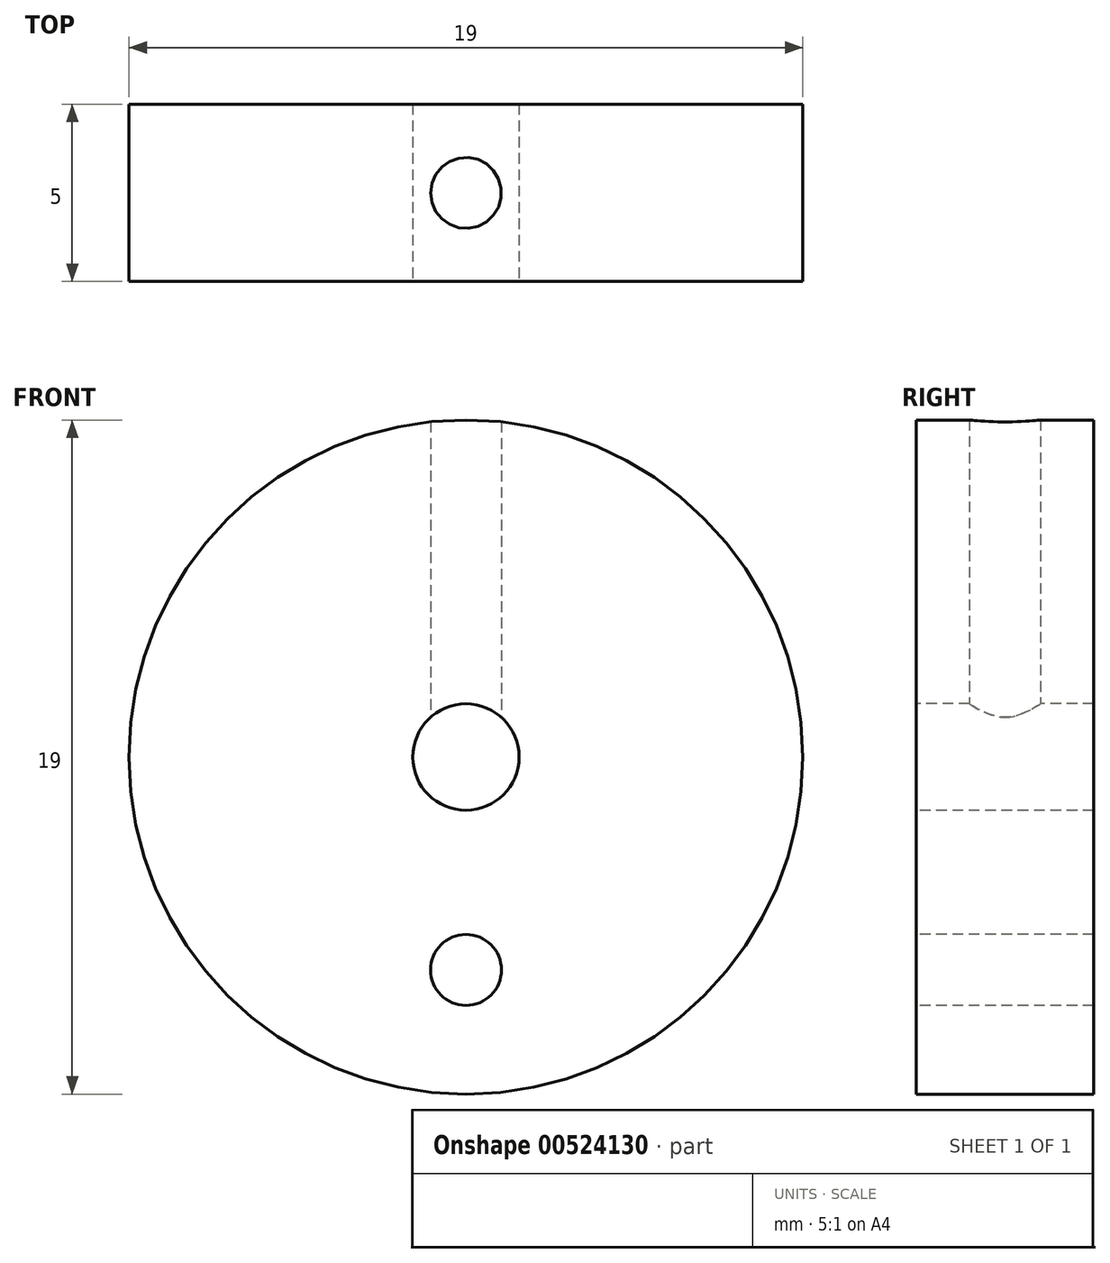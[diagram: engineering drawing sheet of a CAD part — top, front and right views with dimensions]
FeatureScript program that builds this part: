
annotation { "Feature Type Name" : "Feature", "Feature Type Description" : "" }
export const myFeature = defineFeature(function(context is Context, id is Id, definition is map)
    precondition{}
    {
        {
            var Q0;
            Q0=qCreatedBy(makeId("Front.planeOp"),FACE);
            var sketch = newSketch(context, id + "F0", { "sketchPlane" : qUnion([Q0])});
            skCircle(sketch, "E0", {"center": v(0, 0) * mm, "radius": 9.5 * mm});
            skSolve(sketch);
        }
        {
            var Q0;
            Q0=makeQuery(id+"F0.imprint","IMPRINT",FACE,{"disambiguationData":[TD([[makeQuery(id+"F0.imprint","IMPRINT",EDGE,{"derivedFrom":sQuery(id+"F0.wireOp",EDGE,"E0")}),1.0]])]});
            extrude(context, id + "F1", {"entities" : qUnion([Q0]), "oppositeDirection" : true, "depth" : 5 * mm, "offsetDistance" : 25 * mm});
        }
        {
            var Q0;
            Q0=makeQuery(id+"F1.opExtrude","CAP_FACE",FACE,{"disambiguationData":[OSD([sQuery(id+"F0.wireOp",EDGE,"E0")])],"isStart":true});
            var sketch = newSketch(context, id + "F2", { "sketchPlane" : qUnion([Q0])});
            skCircle(sketch, "E1", {"center": v(0, 0) * mm, "radius": 1.5 * mm});
            skCircle(sketch, "E2", {"center": v(0, -6) * mm, "radius": 1 * mm});
            skSolve(sketch);
        }
        {
            var Q0;
            Q0=makeQuery(id+"F2.imprint","IMPRINT",FACE,{"disambiguationData":[TD([[makeQuery(id+"F2.imprint","IMPRINT",EDGE,{"derivedFrom":sQuery(id+"F2.wireOp",EDGE,"E1")}),1.0]])]});
            var Q1;
            Q1=makeQuery(id+"F2.imprint","IMPRINT",FACE,{"disambiguationData":[TD([[makeQuery(id+"F2.imprint","IMPRINT",EDGE,{"derivedFrom":sQuery(id+"F2.wireOp",EDGE,"E2")}),1.0]])]});
            extrude(context, id + "F3", {"entities" : qUnion([Q0, Q1]), "operationType" : NewBodyOperationType.REMOVE, "endBound" : BoundingType.THROUGH_ALL, "oppositeDirection" : true, "depth" : 25 * mm, "offsetDistance" : 25 * mm});
        }
        {
            var Q0;
            Q0=qCreatedBy(makeId("Top.planeOp"),FACE);
            var sketch = newSketch(context, id + "F4", { "sketchPlane" : qUnion([Q0])});
            skCircle(sketch, "E3", {"center": v(0, 2.5) * mm, "radius": 1 * mm});
            skSolve(sketch);
        }
        {
            var Q0;
            Q0=makeQuery(id+"F4.imprint","IMPRINT",FACE,{"disambiguationData":[TD([[makeQuery(id+"F4.imprint","IMPRINT",EDGE,{"derivedFrom":sQuery(id+"F4.wireOp",EDGE,"E3")}),1.0]])]});
            extrude(context, id + "F5", {"entities" : qUnion([Q0]), "operationType" : NewBodyOperationType.REMOVE, "depth" : 25 * mm, "offsetDistance" : 25 * mm});
        }
    });
